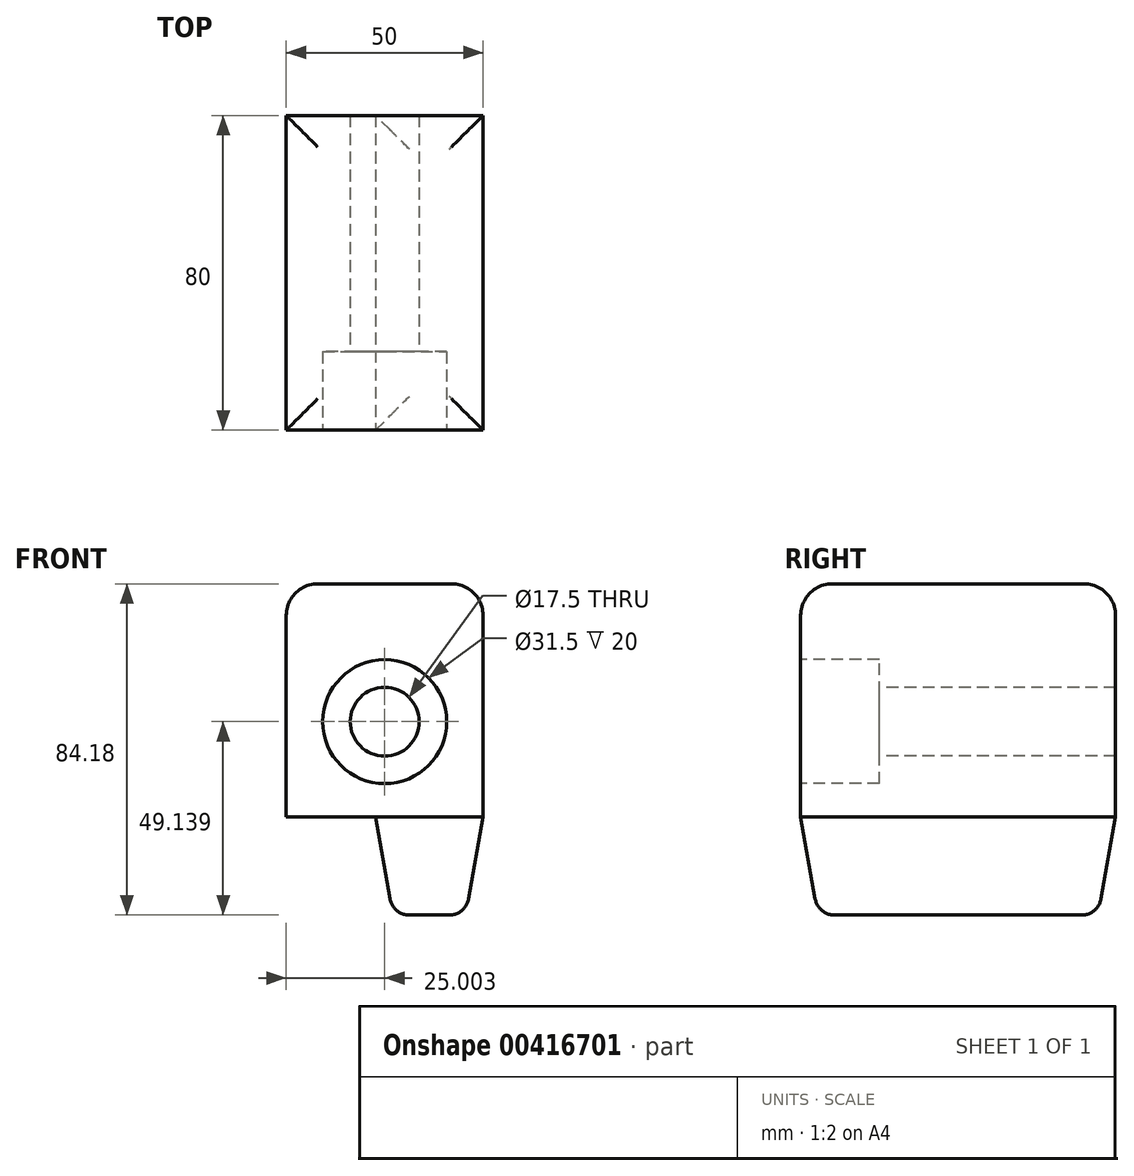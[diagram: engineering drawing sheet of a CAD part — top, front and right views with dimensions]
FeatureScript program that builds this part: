
annotation { "Feature Type Name" : "Feature", "Feature Type Description" : "" }
export const myFeature = defineFeature(function(context is Context, id is Id, definition is map)
    precondition{}
    {
        {
            var Q0;
            Q0=qCreatedBy(makeId("Top.planeOp"),FACE);
            var sketch = newSketch(context, id + "F0", { "sketchPlane" : qUnion([Q0])});
            skLineSegment(sketch, "E0.bottom", {"start": v(-22.67, -17.07) * mm, "end": v(27.33, -17.07) * mm});
            skLineSegment(sketch, "E0.top", {"start": v(-22.67, 62.93) * mm, "end": v(27.33, 62.93) * mm});
            skLineSegment(sketch, "E0.left", {"start": v(-22.67, -17.07) * mm, "end": v(-22.67, 62.93) * mm});
            skLineSegment(sketch, "E0.right", {"start": v(27.33, -17.07) * mm, "end": v(27.33, 62.93) * mm});
            skSolve(sketch);
        }
        {
            var Q0;
            Q0 = qSketchRegion(id + "F0", true);
            extrude(context, id + "F1", {"entities" : qUnion([Q0]), "depth" : 59.18 * mm});
        }
        {
            var Q0;
            Q0=makeQuery(id+"F1.opExtrude","CAP_EDGE",EDGE,{"disambiguationData":[OSD([sQuery(id+"F0.wireOp",EDGE,"E0.left")])],"isStart":false});
            var Q1;
            Q1=makeQuery(id+"F1.opExtrude","CAP_EDGE",EDGE,{"disambiguationData":[OSD([sQuery(id+"F0.wireOp",EDGE,"E0.bottom")])],"isStart":false});
            var Q2;
            Q2=makeQuery(id+"F1.opExtrude","CAP_EDGE",EDGE,{"disambiguationData":[OSD([sQuery(id+"F0.wireOp",EDGE,"E0.right")])],"isStart":false});
            var Q3;
            Q3=makeQuery(id+"F1.opExtrude","CAP_EDGE",EDGE,{"disambiguationData":[OSD([sQuery(id+"F0.wireOp",EDGE,"E0.top")])],"isStart":false});
            fillet(context, id + "F2", {"entities" : qUnion([Q0, Q1, Q2, Q3]), "radius" : 8 * mm, "tangentPropagation" : true, "allowEdgeOverflow" : false});
        }
        {
            var Q0;
            Q0=makeQuery(id+"F1.opExtrude","SWEPT_FACE",FACE,{"disambiguationData":[OSD([sQuery(id+"F0.wireOp",EDGE,"E0.bottom")])]});
            var sketch = newSketch(context, id + "F3", { "sketchPlane" : qUnion([Q0])});
            skLineSegment(sketch, "E1", {"start": v(2.33, 0) * mm, "end": v(2.33, 24.14) * mm, "construction": true});
            skSolve(sketch);
        }
        {
            var Q0;
            Q0=sQuery(id+"F3.wireOp",VERTEX,"E1.end");
            var Q1;
            Q1=makeQuery(id+"F1.opExtrude","SWEPT_BODY",BODY,{"disambiguationData":[OSD([sQuery(id+"F0.wireOp",EDGE,"E0.bottom"),sQuery(id+"F0.wireOp",EDGE,"E0.top"),sQuery(id+"F0.wireOp",EDGE,"E0.left"),sQuery(id+"F0.wireOp",EDGE,"E0.right")])]});
            hole(context, id + "F4", {"style" : HoleStyle.C_BORE, "endStyle" : HoleEndStyle.THROUGH, "standardTappedOrClearance" : lookupTablePath({ "standard" : "ISO", "engagement" : "75%", "pitch" : "2.5 mm", "size" : "M20", "type" : "Tapped" }), "standardBlindInLast" : lookupTablePath({ "standard" : "ISO", "engagement" : "75%", "pitch" : "2.5 mm", "size" : "M20", "type" : "Tapped" }), "holeDiameter" : 17.5 * mm, "cBoreDiameter" : 31.5 * mm, "cBoreDepth" : 20 * mm, "showTappedDepth" : true, "isTappedThrough" : true, "tappedDepth" : 12 * mm, "tapClearance" : 3, "locations" : qUnion([Q0]), "scope" : qUnion([Q1]), "majorDiameter" : 20 * mm});
        }
        {
            var Q0;
            Q0=makeQuery(id+"F1.opExtrude","CAP_FACE",FACE,{"disambiguationData":[OSD([sQuery(id+"F0.wireOp",EDGE,"E0.bottom"),sQuery(id+"F0.wireOp",EDGE,"E0.top"),sQuery(id+"F0.wireOp",EDGE,"E0.left"),sQuery(id+"F0.wireOp",EDGE,"E0.right")])],"isStart":true});
            var sketch = newSketch(context, id + "F5", { "sketchPlane" : qUnion([Q0])});
            skPoint(sketch, "E2.oppositeSnap0", {"position": v(2.33, -62.93) * mm});
            skLineSegment(sketch, "E2.bottom", {"start": v(27.33, 17.07) * mm, "end": v(0, 17.07) * mm});
            skLineSegment(sketch, "E2.top", {"start": v(27.33, -62.93) * mm, "end": v(0, -62.93) * mm});
            skLineSegment(sketch, "E2.left", {"start": v(27.33, 17.07) * mm, "end": v(27.33, -62.93) * mm});
            skLineSegment(sketch, "E2.right", {"start": v(0, 17.07) * mm, "end": v(0, -62.93) * mm});
            skSolve(sketch);
        }
        {
            var Q0;
            Q0 = qSketchRegion(id + "F5", true);
            extrude(context, id + "F6", {"entities" : qUnion([Q0]), "operationType" : NewBodyOperationType.ADD, "depth" : 25 * mm, "hasDraft" : true, "draftAngle" : 10 * degree, "draftPullDirection" : true});
        }
        {
            var Q0;
            Q0=makeQuery(id+"F6.opExtrude","CAP_FACE",FACE,{"disambiguationData":[OSD([sQuery(id+"F5.wireOp",EDGE,"E2.bottom"),sQuery(id+"F5.wireOp",EDGE,"E2.top"),sQuery(id+"F5.wireOp",EDGE,"E2.left"),sQuery(id+"F5.wireOp",EDGE,"E2.right")])],"isStart":false});
            fillet(context, id + "F7", {"entities" : qUnion([Q0]), "radius" : 5 * mm, "tangentPropagation" : true, "allowEdgeOverflow" : false});
        }
    });
